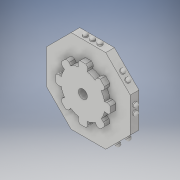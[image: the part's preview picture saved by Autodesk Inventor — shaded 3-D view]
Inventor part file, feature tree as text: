
AUTODESK INVENTOR PART (.ipt)
format: ipt  version: 2017 (Build 210142000, 142)  size: 351,232 bytes
history: native  units: in
note: dims shown in document units (in); Inventor stores cm internally (conversion verified against a paired STEP export)
features: sketch x11, extrude x10, fillet x7, pattern_circular x1
ambient origin geometry x8: Origin, YZ Plane, XZ Plane, XY Plane, X Axis, Y Axis, Z Axis, Center Point
bodies: Solid1 (feature_tree)
feature tree (29):
  extrude  "Extrusion1"  Depth=0.1181in TaperAngle=0.0deg
  extrude  "Extrusion2"  Depth=0.1in
  fillet  "Fillet1"  Radius=0.1in
  sketch  "Sketch3"  dims[d8=0.063in d9=0.063in d10=0.059in]
  sketch  "Sketch4"  dims[d11=0.0472in d12=0.0in d13=0.0315in d24=0.059in]
  sketch  "Sketch5"  dims[d25=0.063in d26=0.1in d27=0.1in d28=0.063in d29=0.063in d31=0.0575in d32=0.059in d34=0.0in d35=0.059in]
  sketch  "Sketch6"  dims[d36=0.059in]
  sketch  "Sketch7"  dims[d40=0.063in d41=0.1in d42=0.1in d43=0.063in d44=0.063in d46=0.059in d47=0.0in d48=0.059in d49=0.059in d50=0.0in d51=0.0in]
  sketch  "Sketch8"  dims[d70=0.063in d71=0.1in d72=0.1in d73=0.063in d74=0.063in d76=0.059in d77=0.0in d78=0.059in d79=0.059in d81=0.0in d82=0.0in]
  sketch  "Sketch9"  dims[d83=0.063in d84=0.1in d85=0.1in d86=0.063in d87=0.063in d89=0.059in d90=0.059in d91=0.059in d92=0.0in d93=0.0in d94=0.0in d95=0.0in]
  extrude  "Extrusion6"  Depth=0.063in
  fillet  "Fillet5"  Radius=0.059in
  extrude  "Extrusion7"  Depth=0.0315in
  fillet  "Fillet6"  Radius=0.059in
  extrude  "Extrusion8"  TaperAngle=0.0deg  [1 undecoded]
  fillet  "Fillet7"  Radius=0.059in
  extrude  "Extrusion9"  TaperAngle=0.0deg  [1 undecoded]
  fillet  "Fillet8"  [1 undecoded]
  extrude  "Extrusion10"  TaperAngle=0.0deg  [1 undecoded]
  fillet  "Fillet9"  [1 undecoded]
  extrude  "Extrusion11"  TaperAngle=0.0deg  [1 undecoded]
  fillet  "Fillet10"  [1 undecoded]
  extrude  "Extrusion14"  Depth=0.0315in
  pattern_circular  "Circular Pattern4"  [2 undecoded]
  extrude  "Extrusion15"  Depth=0.0315in
  sketch  "Sketch1"  dims[d2=0.4724in d3=0.1181in d4=0.0in]
  sketch  "Sketch2"  dims[d5=0.063in d6=0.1in d7=0.1in]
  sketch  "Sketch11"  dims[d96=0.063in d97=0.1in d98=0.1in d99=0.063in d100=0.063in d102=0.059in d103=0.059in d104=0.059in d105=0.0in d106=0.0in d107=0.0in d108=0.0in]
  sketch  "Sketch12"  dims[d109=0.063in d110=0.1in d111=0.1in d112=0.063in d113=0.063in d115=0.059in d116=0.059in d117=0.059in d118=0.0in d119=0.0in d120=0.0in d121=0.0in d122=0.0472in d123=0.0in d124=0.0315in d125=0.0472in d126=0.0in d127=0.0315in d128=0.0472in d129=0.0in d130=0.0315in d131=0.0472in d132=0.0in d133=0.0315in d134=0.0472in d135=0.0in d136=0.0315in d137=0.0472in d138=0.0in d139=0.0315in d148=0.6in d154=12.5984in d156=360.0deg d161=0.04in d162=0.04in d163=0.075in d164=0.0in d165=3.1496in d166=360.0deg d168=0.075in d169=0.236in d170=0.236in d171=0.236in d172=0.236in d173=0.236in d175=0.236in d176=0.236in d177=0.122in d178=1.0in d179=0.0in]
note: 9 required parameter values undecoded (feature->parameter linkage not recoverable at this tier; creation-order binding heuristic only, values carry confidence <= 0.55)
